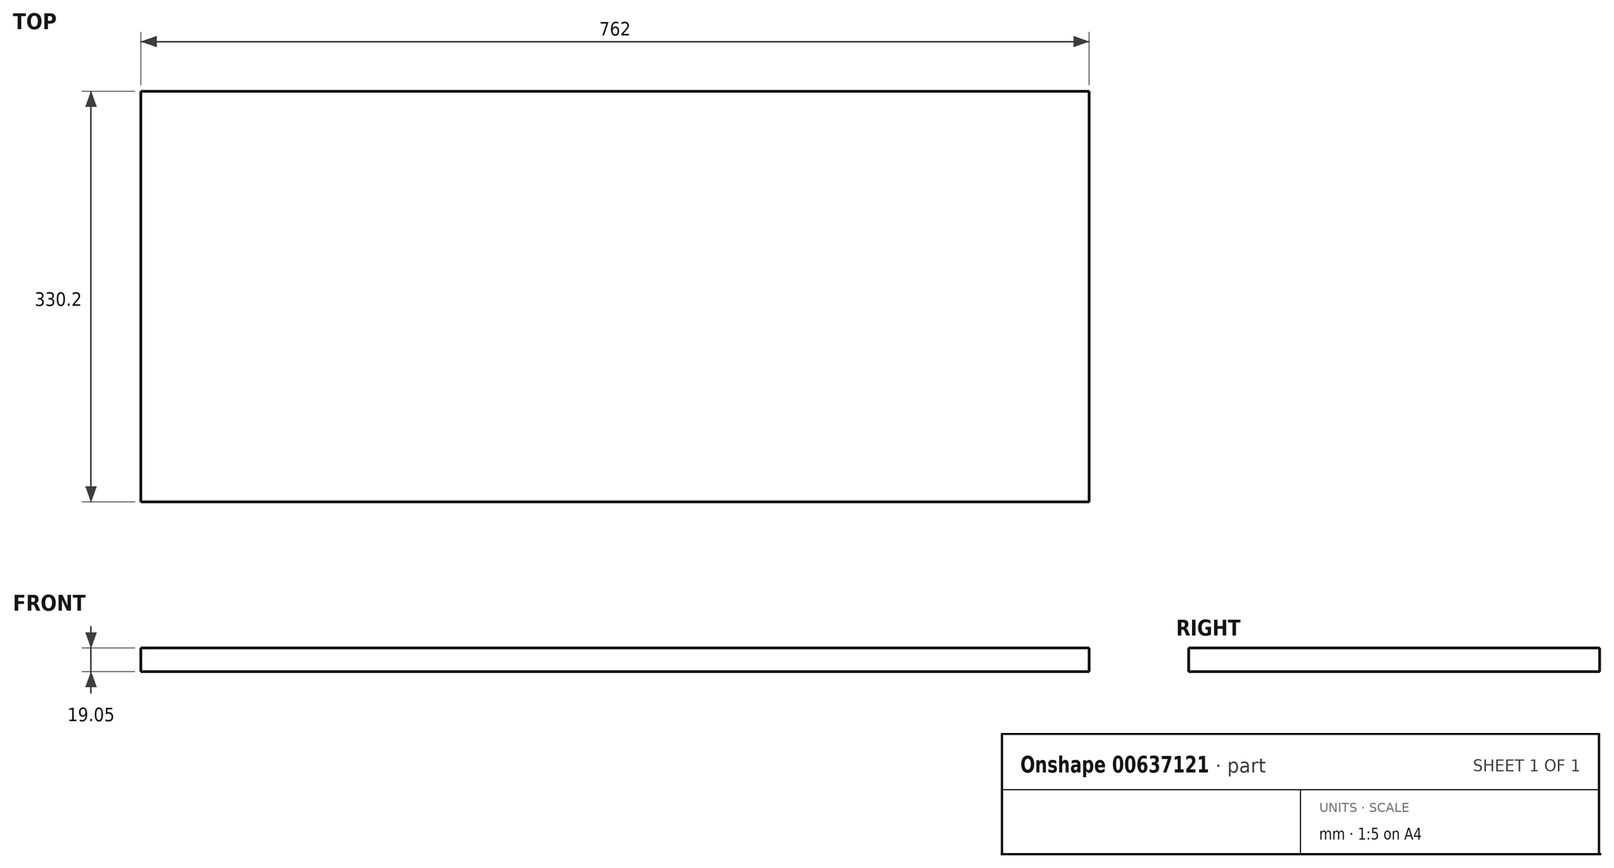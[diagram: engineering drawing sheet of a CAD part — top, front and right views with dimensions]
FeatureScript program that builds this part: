
annotation { "Feature Type Name" : "Feature", "Feature Type Description" : "" }
export const myFeature = defineFeature(function(context is Context, id is Id, definition is map)
    precondition{}
    {
        {
            var Q0;
            Q0=qCreatedBy(makeId("Top.planeOp"),FACE);
            var sketch = newSketch(context, id + "F0", { "sketchPlane" : qUnion([Q0])});
            skLineSegment(sketch, "E0.bottom", {"start": v(-381, 165.1) * mm, "end": v(381, 165.1) * mm});
            skLineSegment(sketch, "E0.top", {"start": v(-381, -165.1) * mm, "end": v(381, -165.1) * mm});
            skLineSegment(sketch, "E0.left", {"start": v(-381, 165.1) * mm, "end": v(-381, -165.1) * mm});
            skLineSegment(sketch, "E0.right", {"start": v(381, 165.1) * mm, "end": v(381, -165.1) * mm});
            skPoint(sketch, "E0.middle", {"position": v(0, 0) * mm});
            skSolve(sketch);
        }
        {
            var Q0;
            Q0=makeQuery(id+"F0.imprint","IMPRINT",FACE,{"disambiguationData":[TD([[makeQuery(id+"F0.imprint","IMPRINT",EDGE,{"derivedFrom":sQuery(id+"F0.wireOp",EDGE,"E0.bottom")}),-1.0]])]});
            extrude(context, id + "F1", {"entities" : qUnion([Q0]), "depth" : 19.05 * mm, "offsetDistance" : 25.4 * mm});
        }
    });
